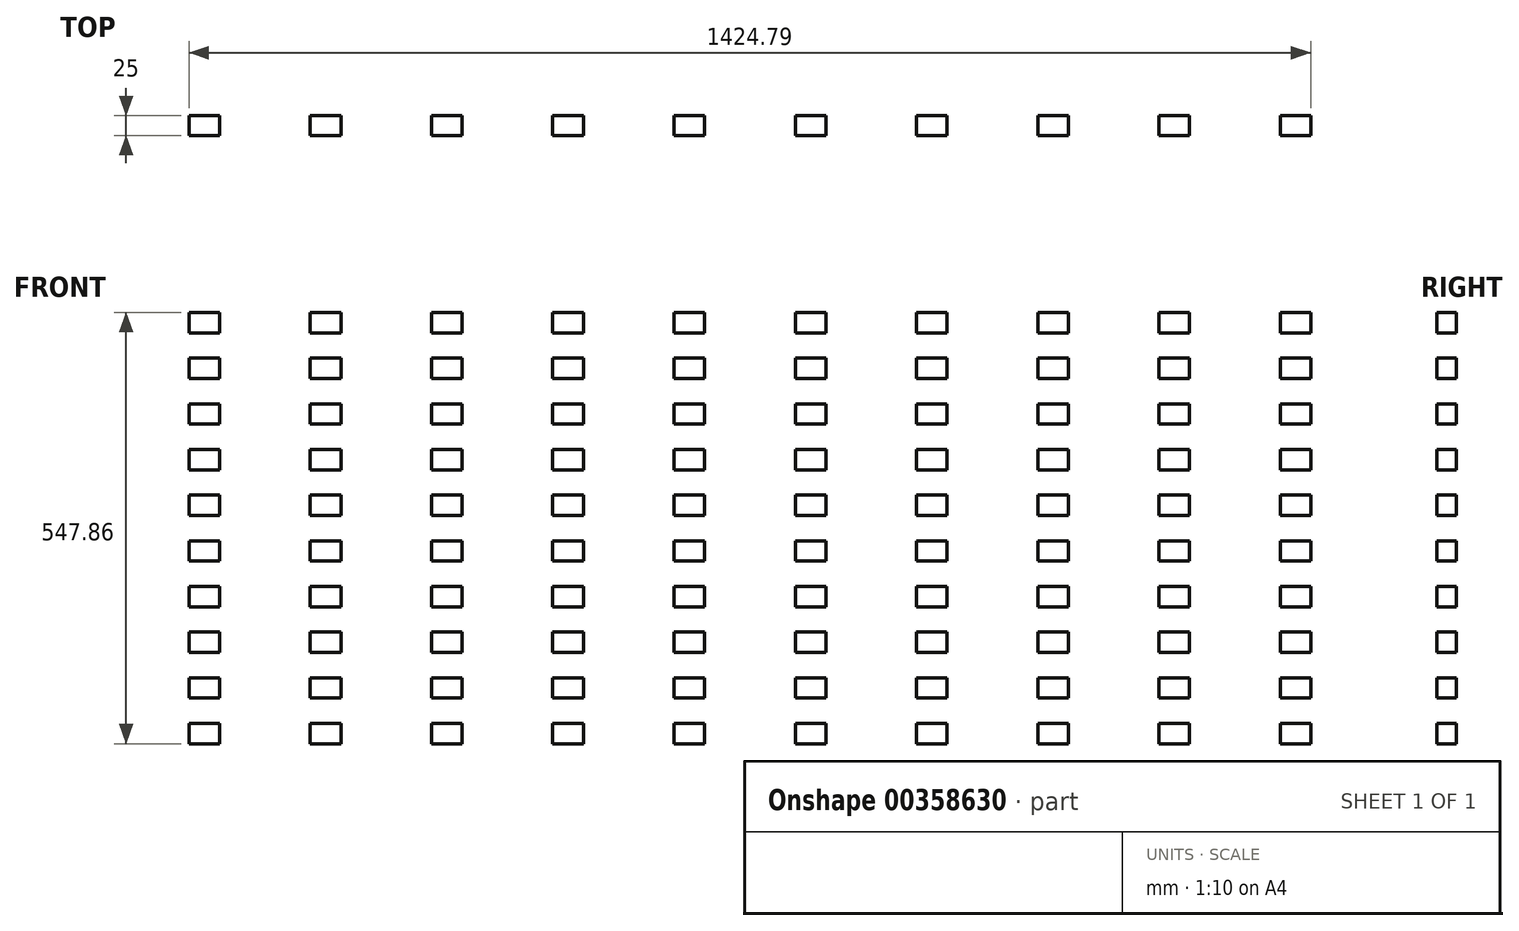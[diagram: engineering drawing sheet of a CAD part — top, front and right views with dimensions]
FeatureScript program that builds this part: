
annotation { "Feature Type Name" : "Feature", "Feature Type Description" : "" }
export const myFeature = defineFeature(function(context is Context, id is Id, definition is map)
    precondition{}
    {
        {
            var Q0;
            Q0=qCreatedBy(makeId("Front.planeOp"),FACE);
            var sketch = newSketch(context, id + "F0", { "sketchPlane" : qUnion([Q0])});
            skLineSegment(sketch, "E0.bottom", {"start": v(-176.52, 30.36) * mm, "end": v(-137.73, 30.36) * mm});
            skLineSegment(sketch, "E0.top", {"start": v(-176.52, 4.5) * mm, "end": v(-137.73, 4.5) * mm});
            skLineSegment(sketch, "E0.left", {"start": v(-176.52, 30.36) * mm, "end": v(-176.52, 4.5) * mm});
            skLineSegment(sketch, "E0.right", {"start": v(-137.73, 30.36) * mm, "end": v(-137.73, 4.5) * mm});
            skLineSegment(sketch, "E1.0.1.0", {"start": v(-176.52, 88.36) * mm, "end": v(-137.73, 88.36) * mm});
            skLineSegment(sketch, "E1.0.1.1", {"start": v(-176.52, 62.5) * mm, "end": v(-137.73, 62.5) * mm});
            skLineSegment(sketch, "E1.0.1.2", {"start": v(-176.52, 88.36) * mm, "end": v(-176.52, 62.5) * mm});
            skLineSegment(sketch, "E1.0.1.3", {"start": v(-137.73, 88.36) * mm, "end": v(-137.73, 62.5) * mm});
            skLineSegment(sketch, "E1.0.2.0", {"start": v(-176.52, 146.36) * mm, "end": v(-137.73, 146.36) * mm});
            skLineSegment(sketch, "E1.0.2.1", {"start": v(-176.52, 120.5) * mm, "end": v(-137.73, 120.5) * mm});
            skLineSegment(sketch, "E1.0.2.2", {"start": v(-176.52, 146.36) * mm, "end": v(-176.52, 120.5) * mm});
            skLineSegment(sketch, "E1.0.2.3", {"start": v(-137.73, 146.36) * mm, "end": v(-137.73, 120.5) * mm});
            skLineSegment(sketch, "E1.0.3.0", {"start": v(-176.52, 204.36) * mm, "end": v(-137.73, 204.36) * mm});
            skLineSegment(sketch, "E1.0.3.1", {"start": v(-176.52, 178.5) * mm, "end": v(-137.73, 178.5) * mm});
            skLineSegment(sketch, "E1.0.3.2", {"start": v(-176.52, 204.36) * mm, "end": v(-176.52, 178.5) * mm});
            skLineSegment(sketch, "E1.0.3.3", {"start": v(-137.73, 204.36) * mm, "end": v(-137.73, 178.5) * mm});
            skLineSegment(sketch, "E1.0.4.0", {"start": v(-176.52, 262.36) * mm, "end": v(-137.73, 262.36) * mm});
            skLineSegment(sketch, "E1.0.4.1", {"start": v(-176.52, 236.5) * mm, "end": v(-137.73, 236.5) * mm});
            skLineSegment(sketch, "E1.0.4.2", {"start": v(-176.52, 262.36) * mm, "end": v(-176.52, 236.5) * mm});
            skLineSegment(sketch, "E1.0.4.3", {"start": v(-137.73, 262.36) * mm, "end": v(-137.73, 236.5) * mm});
            skLineSegment(sketch, "E1.0.5.0", {"start": v(-176.52, 320.36) * mm, "end": v(-137.73, 320.36) * mm});
            skLineSegment(sketch, "E1.0.5.1", {"start": v(-176.52, 294.5) * mm, "end": v(-137.73, 294.5) * mm});
            skLineSegment(sketch, "E1.0.5.2", {"start": v(-176.52, 320.36) * mm, "end": v(-176.52, 294.5) * mm});
            skLineSegment(sketch, "E1.0.5.3", {"start": v(-137.73, 320.36) * mm, "end": v(-137.73, 294.5) * mm});
            skLineSegment(sketch, "E1.0.6.0", {"start": v(-176.52, 378.36) * mm, "end": v(-137.73, 378.36) * mm});
            skLineSegment(sketch, "E1.0.6.1", {"start": v(-176.52, 352.5) * mm, "end": v(-137.73, 352.5) * mm});
            skLineSegment(sketch, "E1.0.6.2", {"start": v(-176.52, 378.36) * mm, "end": v(-176.52, 352.5) * mm});
            skLineSegment(sketch, "E1.0.6.3", {"start": v(-137.73, 378.36) * mm, "end": v(-137.73, 352.5) * mm});
            skLineSegment(sketch, "E1.0.7.0", {"start": v(-176.52, 436.36) * mm, "end": v(-137.73, 436.36) * mm});
            skLineSegment(sketch, "E1.0.7.1", {"start": v(-176.52, 410.5) * mm, "end": v(-137.73, 410.5) * mm});
            skLineSegment(sketch, "E1.0.7.2", {"start": v(-176.52, 436.36) * mm, "end": v(-176.52, 410.5) * mm});
            skLineSegment(sketch, "E1.0.7.3", {"start": v(-137.73, 436.36) * mm, "end": v(-137.73, 410.5) * mm});
            skLineSegment(sketch, "E1.0.8.0", {"start": v(-176.52, 494.36) * mm, "end": v(-137.73, 494.36) * mm});
            skLineSegment(sketch, "E1.0.8.1", {"start": v(-176.52, 468.5) * mm, "end": v(-137.73, 468.5) * mm});
            skLineSegment(sketch, "E1.0.8.2", {"start": v(-176.52, 494.36) * mm, "end": v(-176.52, 468.5) * mm});
            skLineSegment(sketch, "E1.0.8.3", {"start": v(-137.73, 494.36) * mm, "end": v(-137.73, 468.5) * mm});
            skLineSegment(sketch, "E1.0.9.0", {"start": v(-176.52, 552.36) * mm, "end": v(-137.73, 552.36) * mm});
            skLineSegment(sketch, "E1.0.9.1", {"start": v(-176.52, 526.5) * mm, "end": v(-137.73, 526.5) * mm});
            skLineSegment(sketch, "E1.0.9.2", {"start": v(-176.52, 552.36) * mm, "end": v(-176.52, 526.5) * mm});
            skLineSegment(sketch, "E1.0.9.3", {"start": v(-137.73, 552.36) * mm, "end": v(-137.73, 526.5) * mm});
            skLineSegment(sketch, "E1.1.0.0", {"start": v(-22.52, 30.36) * mm, "end": v(16.27, 30.36) * mm});
            skLineSegment(sketch, "E1.1.0.1", {"start": v(-22.52, 4.5) * mm, "end": v(16.27, 4.5) * mm});
            skLineSegment(sketch, "E1.1.0.2", {"start": v(-22.52, 30.36) * mm, "end": v(-22.52, 4.5) * mm});
            skLineSegment(sketch, "E1.1.0.3", {"start": v(16.27, 30.36) * mm, "end": v(16.27, 4.5) * mm});
            skLineSegment(sketch, "E1.1.1.0", {"start": v(-22.52, 88.36) * mm, "end": v(16.27, 88.36) * mm});
            skLineSegment(sketch, "E1.1.1.1", {"start": v(-22.52, 62.5) * mm, "end": v(16.27, 62.5) * mm});
            skLineSegment(sketch, "E1.1.1.2", {"start": v(-22.52, 88.36) * mm, "end": v(-22.52, 62.5) * mm});
            skLineSegment(sketch, "E1.1.1.3", {"start": v(16.27, 88.36) * mm, "end": v(16.27, 62.5) * mm});
            skLineSegment(sketch, "E1.1.2.0", {"start": v(-22.52, 146.36) * mm, "end": v(16.27, 146.36) * mm});
            skLineSegment(sketch, "E1.1.2.1", {"start": v(-22.52, 120.5) * mm, "end": v(16.27, 120.5) * mm});
            skLineSegment(sketch, "E1.1.2.2", {"start": v(-22.52, 146.36) * mm, "end": v(-22.52, 120.5) * mm});
            skLineSegment(sketch, "E1.1.2.3", {"start": v(16.27, 146.36) * mm, "end": v(16.27, 120.5) * mm});
            skLineSegment(sketch, "E1.1.3.0", {"start": v(-22.52, 204.36) * mm, "end": v(16.27, 204.36) * mm});
            skLineSegment(sketch, "E1.1.3.1", {"start": v(-22.52, 178.5) * mm, "end": v(16.27, 178.5) * mm});
            skLineSegment(sketch, "E1.1.3.2", {"start": v(-22.52, 204.36) * mm, "end": v(-22.52, 178.5) * mm});
            skLineSegment(sketch, "E1.1.3.3", {"start": v(16.27, 204.36) * mm, "end": v(16.27, 178.5) * mm});
            skLineSegment(sketch, "E1.1.4.0", {"start": v(-22.52, 262.36) * mm, "end": v(16.27, 262.36) * mm});
            skLineSegment(sketch, "E1.1.4.1", {"start": v(-22.52, 236.5) * mm, "end": v(16.27, 236.5) * mm});
            skLineSegment(sketch, "E1.1.4.2", {"start": v(-22.52, 262.36) * mm, "end": v(-22.52, 236.5) * mm});
            skLineSegment(sketch, "E1.1.4.3", {"start": v(16.27, 262.36) * mm, "end": v(16.27, 236.5) * mm});
            skLineSegment(sketch, "E1.1.5.0", {"start": v(-22.52, 320.36) * mm, "end": v(16.27, 320.36) * mm});
            skLineSegment(sketch, "E1.1.5.1", {"start": v(-22.52, 294.5) * mm, "end": v(16.27, 294.5) * mm});
            skLineSegment(sketch, "E1.1.5.2", {"start": v(-22.52, 320.36) * mm, "end": v(-22.52, 294.5) * mm});
            skLineSegment(sketch, "E1.1.5.3", {"start": v(16.27, 320.36) * mm, "end": v(16.27, 294.5) * mm});
            skLineSegment(sketch, "E1.1.6.0", {"start": v(-22.52, 378.36) * mm, "end": v(16.27, 378.36) * mm});
            skLineSegment(sketch, "E1.1.6.1", {"start": v(-22.52, 352.5) * mm, "end": v(16.27, 352.5) * mm});
            skLineSegment(sketch, "E1.1.6.2", {"start": v(-22.52, 378.36) * mm, "end": v(-22.52, 352.5) * mm});
            skLineSegment(sketch, "E1.1.6.3", {"start": v(16.27, 378.36) * mm, "end": v(16.27, 352.5) * mm});
            skLineSegment(sketch, "E1.1.7.0", {"start": v(-22.52, 436.36) * mm, "end": v(16.27, 436.36) * mm});
            skLineSegment(sketch, "E1.1.7.1", {"start": v(-22.52, 410.5) * mm, "end": v(16.27, 410.5) * mm});
            skLineSegment(sketch, "E1.1.7.2", {"start": v(-22.52, 436.36) * mm, "end": v(-22.52, 410.5) * mm});
            skLineSegment(sketch, "E1.1.7.3", {"start": v(16.27, 436.36) * mm, "end": v(16.27, 410.5) * mm});
            skLineSegment(sketch, "E1.1.8.0", {"start": v(-22.52, 494.36) * mm, "end": v(16.27, 494.36) * mm});
            skLineSegment(sketch, "E1.1.8.1", {"start": v(-22.52, 468.5) * mm, "end": v(16.27, 468.5) * mm});
            skLineSegment(sketch, "E1.1.8.2", {"start": v(-22.52, 494.36) * mm, "end": v(-22.52, 468.5) * mm});
            skLineSegment(sketch, "E1.1.8.3", {"start": v(16.27, 494.36) * mm, "end": v(16.27, 468.5) * mm});
            skLineSegment(sketch, "E1.1.9.0", {"start": v(-22.52, 552.36) * mm, "end": v(16.27, 552.36) * mm});
            skLineSegment(sketch, "E1.1.9.1", {"start": v(-22.52, 526.5) * mm, "end": v(16.27, 526.5) * mm});
            skLineSegment(sketch, "E1.1.9.2", {"start": v(-22.52, 552.36) * mm, "end": v(-22.52, 526.5) * mm});
            skLineSegment(sketch, "E1.1.9.3", {"start": v(16.27, 552.36) * mm, "end": v(16.27, 526.5) * mm});
            skLineSegment(sketch, "E1.2.0.0", {"start": v(131.48, 30.36) * mm, "end": v(170.27, 30.36) * mm});
            skLineSegment(sketch, "E1.2.0.1", {"start": v(131.48, 4.5) * mm, "end": v(170.27, 4.5) * mm});
            skLineSegment(sketch, "E1.2.0.2", {"start": v(131.48, 30.36) * mm, "end": v(131.48, 4.5) * mm});
            skLineSegment(sketch, "E1.2.0.3", {"start": v(170.27, 30.36) * mm, "end": v(170.27, 4.5) * mm});
            skLineSegment(sketch, "E1.2.1.0", {"start": v(131.48, 88.36) * mm, "end": v(170.27, 88.36) * mm});
            skLineSegment(sketch, "E1.2.1.1", {"start": v(131.48, 62.5) * mm, "end": v(170.27, 62.5) * mm});
            skLineSegment(sketch, "E1.2.1.2", {"start": v(131.48, 88.36) * mm, "end": v(131.48, 62.5) * mm});
            skLineSegment(sketch, "E1.2.1.3", {"start": v(170.27, 88.36) * mm, "end": v(170.27, 62.5) * mm});
            skLineSegment(sketch, "E1.2.2.0", {"start": v(131.48, 146.36) * mm, "end": v(170.27, 146.36) * mm});
            skLineSegment(sketch, "E1.2.2.1", {"start": v(131.48, 120.5) * mm, "end": v(170.27, 120.5) * mm});
            skLineSegment(sketch, "E1.2.2.2", {"start": v(131.48, 146.36) * mm, "end": v(131.48, 120.5) * mm});
            skLineSegment(sketch, "E1.2.2.3", {"start": v(170.27, 146.36) * mm, "end": v(170.27, 120.5) * mm});
            skLineSegment(sketch, "E1.2.3.0", {"start": v(131.48, 204.36) * mm, "end": v(170.27, 204.36) * mm});
            skLineSegment(sketch, "E1.2.3.1", {"start": v(131.48, 178.5) * mm, "end": v(170.27, 178.5) * mm});
            skLineSegment(sketch, "E1.2.3.2", {"start": v(131.48, 204.36) * mm, "end": v(131.48, 178.5) * mm});
            skLineSegment(sketch, "E1.2.3.3", {"start": v(170.27, 204.36) * mm, "end": v(170.27, 178.5) * mm});
            skLineSegment(sketch, "E1.2.4.0", {"start": v(131.48, 262.36) * mm, "end": v(170.27, 262.36) * mm});
            skLineSegment(sketch, "E1.2.4.1", {"start": v(131.48, 236.5) * mm, "end": v(170.27, 236.5) * mm});
            skLineSegment(sketch, "E1.2.4.2", {"start": v(131.48, 262.36) * mm, "end": v(131.48, 236.5) * mm});
            skLineSegment(sketch, "E1.2.4.3", {"start": v(170.27, 262.36) * mm, "end": v(170.27, 236.5) * mm});
            skLineSegment(sketch, "E1.2.5.0", {"start": v(131.48, 320.36) * mm, "end": v(170.27, 320.36) * mm});
            skLineSegment(sketch, "E1.2.5.1", {"start": v(131.48, 294.5) * mm, "end": v(170.27, 294.5) * mm});
            skLineSegment(sketch, "E1.2.5.2", {"start": v(131.48, 320.36) * mm, "end": v(131.48, 294.5) * mm});
            skLineSegment(sketch, "E1.2.5.3", {"start": v(170.27, 320.36) * mm, "end": v(170.27, 294.5) * mm});
            skLineSegment(sketch, "E1.2.6.0", {"start": v(131.48, 378.36) * mm, "end": v(170.27, 378.36) * mm});
            skLineSegment(sketch, "E1.2.6.1", {"start": v(131.48, 352.5) * mm, "end": v(170.27, 352.5) * mm});
            skLineSegment(sketch, "E1.2.6.2", {"start": v(131.48, 378.36) * mm, "end": v(131.48, 352.5) * mm});
            skLineSegment(sketch, "E1.2.6.3", {"start": v(170.27, 378.36) * mm, "end": v(170.27, 352.5) * mm});
            skLineSegment(sketch, "E1.2.7.0", {"start": v(131.48, 436.36) * mm, "end": v(170.27, 436.36) * mm});
            skLineSegment(sketch, "E1.2.7.1", {"start": v(131.48, 410.5) * mm, "end": v(170.27, 410.5) * mm});
            skLineSegment(sketch, "E1.2.7.2", {"start": v(131.48, 436.36) * mm, "end": v(131.48, 410.5) * mm});
            skLineSegment(sketch, "E1.2.7.3", {"start": v(170.27, 436.36) * mm, "end": v(170.27, 410.5) * mm});
            skLineSegment(sketch, "E1.2.8.0", {"start": v(131.48, 494.36) * mm, "end": v(170.27, 494.36) * mm});
            skLineSegment(sketch, "E1.2.8.1", {"start": v(131.48, 468.5) * mm, "end": v(170.27, 468.5) * mm});
            skLineSegment(sketch, "E1.2.8.2", {"start": v(131.48, 494.36) * mm, "end": v(131.48, 468.5) * mm});
            skLineSegment(sketch, "E1.2.8.3", {"start": v(170.27, 494.36) * mm, "end": v(170.27, 468.5) * mm});
            skLineSegment(sketch, "E1.2.9.0", {"start": v(131.48, 552.36) * mm, "end": v(170.27, 552.36) * mm});
            skLineSegment(sketch, "E1.2.9.1", {"start": v(131.48, 526.5) * mm, "end": v(170.27, 526.5) * mm});
            skLineSegment(sketch, "E1.2.9.2", {"start": v(131.48, 552.36) * mm, "end": v(131.48, 526.5) * mm});
            skLineSegment(sketch, "E1.2.9.3", {"start": v(170.27, 552.36) * mm, "end": v(170.27, 526.5) * mm});
            skLineSegment(sketch, "E1.3.0.0", {"start": v(285.48, 30.36) * mm, "end": v(324.27, 30.36) * mm});
            skLineSegment(sketch, "E1.3.0.1", {"start": v(285.48, 4.5) * mm, "end": v(324.27, 4.5) * mm});
            skLineSegment(sketch, "E1.3.0.2", {"start": v(285.48, 30.36) * mm, "end": v(285.48, 4.5) * mm});
            skLineSegment(sketch, "E1.3.0.3", {"start": v(324.27, 30.36) * mm, "end": v(324.27, 4.5) * mm});
            skLineSegment(sketch, "E1.3.1.0", {"start": v(285.48, 88.36) * mm, "end": v(324.27, 88.36) * mm});
            skLineSegment(sketch, "E1.3.1.1", {"start": v(285.48, 62.5) * mm, "end": v(324.27, 62.5) * mm});
            skLineSegment(sketch, "E1.3.1.2", {"start": v(285.48, 88.36) * mm, "end": v(285.48, 62.5) * mm});
            skLineSegment(sketch, "E1.3.1.3", {"start": v(324.27, 88.36) * mm, "end": v(324.27, 62.5) * mm});
            skLineSegment(sketch, "E1.3.2.0", {"start": v(285.48, 146.36) * mm, "end": v(324.27, 146.36) * mm});
            skLineSegment(sketch, "E1.3.2.1", {"start": v(285.48, 120.5) * mm, "end": v(324.27, 120.5) * mm});
            skLineSegment(sketch, "E1.3.2.2", {"start": v(285.48, 146.36) * mm, "end": v(285.48, 120.5) * mm});
            skLineSegment(sketch, "E1.3.2.3", {"start": v(324.27, 146.36) * mm, "end": v(324.27, 120.5) * mm});
            skLineSegment(sketch, "E1.3.3.0", {"start": v(285.48, 204.36) * mm, "end": v(324.27, 204.36) * mm});
            skLineSegment(sketch, "E1.3.3.1", {"start": v(285.48, 178.5) * mm, "end": v(324.27, 178.5) * mm});
            skLineSegment(sketch, "E1.3.3.2", {"start": v(285.48, 204.36) * mm, "end": v(285.48, 178.5) * mm});
            skLineSegment(sketch, "E1.3.3.3", {"start": v(324.27, 204.36) * mm, "end": v(324.27, 178.5) * mm});
            skLineSegment(sketch, "E1.3.4.0", {"start": v(285.48, 262.36) * mm, "end": v(324.27, 262.36) * mm});
            skLineSegment(sketch, "E1.3.4.1", {"start": v(285.48, 236.5) * mm, "end": v(324.27, 236.5) * mm});
            skLineSegment(sketch, "E1.3.4.2", {"start": v(285.48, 262.36) * mm, "end": v(285.48, 236.5) * mm});
            skLineSegment(sketch, "E1.3.4.3", {"start": v(324.27, 262.36) * mm, "end": v(324.27, 236.5) * mm});
            skLineSegment(sketch, "E1.3.5.0", {"start": v(285.48, 320.36) * mm, "end": v(324.27, 320.36) * mm});
            skLineSegment(sketch, "E1.3.5.1", {"start": v(285.48, 294.5) * mm, "end": v(324.27, 294.5) * mm});
            skLineSegment(sketch, "E1.3.5.2", {"start": v(285.48, 320.36) * mm, "end": v(285.48, 294.5) * mm});
            skLineSegment(sketch, "E1.3.5.3", {"start": v(324.27, 320.36) * mm, "end": v(324.27, 294.5) * mm});
            skLineSegment(sketch, "E1.3.6.0", {"start": v(285.48, 378.36) * mm, "end": v(324.27, 378.36) * mm});
            skLineSegment(sketch, "E1.3.6.1", {"start": v(285.48, 352.5) * mm, "end": v(324.27, 352.5) * mm});
            skLineSegment(sketch, "E1.3.6.2", {"start": v(285.48, 378.36) * mm, "end": v(285.48, 352.5) * mm});
            skLineSegment(sketch, "E1.3.6.3", {"start": v(324.27, 378.36) * mm, "end": v(324.27, 352.5) * mm});
            skLineSegment(sketch, "E1.3.7.0", {"start": v(285.48, 436.36) * mm, "end": v(324.27, 436.36) * mm});
            skLineSegment(sketch, "E1.3.7.1", {"start": v(285.48, 410.5) * mm, "end": v(324.27, 410.5) * mm});
            skLineSegment(sketch, "E1.3.7.2", {"start": v(285.48, 436.36) * mm, "end": v(285.48, 410.5) * mm});
            skLineSegment(sketch, "E1.3.7.3", {"start": v(324.27, 436.36) * mm, "end": v(324.27, 410.5) * mm});
            skLineSegment(sketch, "E1.3.8.0", {"start": v(285.48, 494.36) * mm, "end": v(324.27, 494.36) * mm});
            skLineSegment(sketch, "E1.3.8.1", {"start": v(285.48, 468.5) * mm, "end": v(324.27, 468.5) * mm});
            skLineSegment(sketch, "E1.3.8.2", {"start": v(285.48, 494.36) * mm, "end": v(285.48, 468.5) * mm});
            skLineSegment(sketch, "E1.3.8.3", {"start": v(324.27, 494.36) * mm, "end": v(324.27, 468.5) * mm});
            skLineSegment(sketch, "E1.3.9.0", {"start": v(285.48, 552.36) * mm, "end": v(324.27, 552.36) * mm});
            skLineSegment(sketch, "E1.3.9.1", {"start": v(285.48, 526.5) * mm, "end": v(324.27, 526.5) * mm});
            skLineSegment(sketch, "E1.3.9.2", {"start": v(285.48, 552.36) * mm, "end": v(285.48, 526.5) * mm});
            skLineSegment(sketch, "E1.3.9.3", {"start": v(324.27, 552.36) * mm, "end": v(324.27, 526.5) * mm});
            skLineSegment(sketch, "E1.4.0.0", {"start": v(439.48, 30.36) * mm, "end": v(478.27, 30.36) * mm});
            skLineSegment(sketch, "E1.4.0.1", {"start": v(439.48, 4.5) * mm, "end": v(478.27, 4.5) * mm});
            skLineSegment(sketch, "E1.4.0.2", {"start": v(439.48, 30.36) * mm, "end": v(439.48, 4.5) * mm});
            skLineSegment(sketch, "E1.4.0.3", {"start": v(478.27, 30.36) * mm, "end": v(478.27, 4.5) * mm});
            skLineSegment(sketch, "E1.4.1.0", {"start": v(439.48, 88.36) * mm, "end": v(478.27, 88.36) * mm});
            skLineSegment(sketch, "E1.4.1.1", {"start": v(439.48, 62.5) * mm, "end": v(478.27, 62.5) * mm});
            skLineSegment(sketch, "E1.4.1.2", {"start": v(439.48, 88.36) * mm, "end": v(439.48, 62.5) * mm});
            skLineSegment(sketch, "E1.4.1.3", {"start": v(478.27, 88.36) * mm, "end": v(478.27, 62.5) * mm});
            skLineSegment(sketch, "E1.4.2.0", {"start": v(439.48, 146.36) * mm, "end": v(478.27, 146.36) * mm});
            skLineSegment(sketch, "E1.4.2.1", {"start": v(439.48, 120.5) * mm, "end": v(478.27, 120.5) * mm});
            skLineSegment(sketch, "E1.4.2.2", {"start": v(439.48, 146.36) * mm, "end": v(439.48, 120.5) * mm});
            skLineSegment(sketch, "E1.4.2.3", {"start": v(478.27, 146.36) * mm, "end": v(478.27, 120.5) * mm});
            skLineSegment(sketch, "E1.4.3.0", {"start": v(439.48, 204.36) * mm, "end": v(478.27, 204.36) * mm});
            skLineSegment(sketch, "E1.4.3.1", {"start": v(439.48, 178.5) * mm, "end": v(478.27, 178.5) * mm});
            skLineSegment(sketch, "E1.4.3.2", {"start": v(439.48, 204.36) * mm, "end": v(439.48, 178.5) * mm});
            skLineSegment(sketch, "E1.4.3.3", {"start": v(478.27, 204.36) * mm, "end": v(478.27, 178.5) * mm});
            skLineSegment(sketch, "E1.4.4.0", {"start": v(439.48, 262.36) * mm, "end": v(478.27, 262.36) * mm});
            skLineSegment(sketch, "E1.4.4.1", {"start": v(439.48, 236.5) * mm, "end": v(478.27, 236.5) * mm});
            skLineSegment(sketch, "E1.4.4.2", {"start": v(439.48, 262.36) * mm, "end": v(439.48, 236.5) * mm});
            skLineSegment(sketch, "E1.4.4.3", {"start": v(478.27, 262.36) * mm, "end": v(478.27, 236.5) * mm});
            skLineSegment(sketch, "E1.4.5.0", {"start": v(439.48, 320.36) * mm, "end": v(478.27, 320.36) * mm});
            skLineSegment(sketch, "E1.4.5.1", {"start": v(439.48, 294.5) * mm, "end": v(478.27, 294.5) * mm});
            skLineSegment(sketch, "E1.4.5.2", {"start": v(439.48, 320.36) * mm, "end": v(439.48, 294.5) * mm});
            skLineSegment(sketch, "E1.4.5.3", {"start": v(478.27, 320.36) * mm, "end": v(478.27, 294.5) * mm});
            skLineSegment(sketch, "E1.4.6.0", {"start": v(439.48, 378.36) * mm, "end": v(478.27, 378.36) * mm});
            skLineSegment(sketch, "E1.4.6.1", {"start": v(439.48, 352.5) * mm, "end": v(478.27, 352.5) * mm});
            skLineSegment(sketch, "E1.4.6.2", {"start": v(439.48, 378.36) * mm, "end": v(439.48, 352.5) * mm});
            skLineSegment(sketch, "E1.4.6.3", {"start": v(478.27, 378.36) * mm, "end": v(478.27, 352.5) * mm});
            skLineSegment(sketch, "E1.4.7.0", {"start": v(439.48, 436.36) * mm, "end": v(478.27, 436.36) * mm});
            skLineSegment(sketch, "E1.4.7.1", {"start": v(439.48, 410.5) * mm, "end": v(478.27, 410.5) * mm});
            skLineSegment(sketch, "E1.4.7.2", {"start": v(439.48, 436.36) * mm, "end": v(439.48, 410.5) * mm});
            skLineSegment(sketch, "E1.4.7.3", {"start": v(478.27, 436.36) * mm, "end": v(478.27, 410.5) * mm});
            skLineSegment(sketch, "E1.4.8.0", {"start": v(439.48, 494.36) * mm, "end": v(478.27, 494.36) * mm});
            skLineSegment(sketch, "E1.4.8.1", {"start": v(439.48, 468.5) * mm, "end": v(478.27, 468.5) * mm});
            skLineSegment(sketch, "E1.4.8.2", {"start": v(439.48, 494.36) * mm, "end": v(439.48, 468.5) * mm});
            skLineSegment(sketch, "E1.4.8.3", {"start": v(478.27, 494.36) * mm, "end": v(478.27, 468.5) * mm});
            skLineSegment(sketch, "E1.4.9.0", {"start": v(439.48, 552.36) * mm, "end": v(478.27, 552.36) * mm});
            skLineSegment(sketch, "E1.4.9.1", {"start": v(439.48, 526.5) * mm, "end": v(478.27, 526.5) * mm});
            skLineSegment(sketch, "E1.4.9.2", {"start": v(439.48, 552.36) * mm, "end": v(439.48, 526.5) * mm});
            skLineSegment(sketch, "E1.4.9.3", {"start": v(478.27, 552.36) * mm, "end": v(478.27, 526.5) * mm});
            skLineSegment(sketch, "E1.5.0.0", {"start": v(593.48, 30.36) * mm, "end": v(632.27, 30.36) * mm});
            skLineSegment(sketch, "E1.5.0.1", {"start": v(593.48, 4.5) * mm, "end": v(632.27, 4.5) * mm});
            skLineSegment(sketch, "E1.5.0.2", {"start": v(593.48, 30.36) * mm, "end": v(593.48, 4.5) * mm});
            skLineSegment(sketch, "E1.5.0.3", {"start": v(632.27, 30.36) * mm, "end": v(632.27, 4.5) * mm});
            skLineSegment(sketch, "E1.5.1.0", {"start": v(593.48, 88.36) * mm, "end": v(632.27, 88.36) * mm});
            skLineSegment(sketch, "E1.5.1.1", {"start": v(593.48, 62.5) * mm, "end": v(632.27, 62.5) * mm});
            skLineSegment(sketch, "E1.5.1.2", {"start": v(593.48, 88.36) * mm, "end": v(593.48, 62.5) * mm});
            skLineSegment(sketch, "E1.5.1.3", {"start": v(632.27, 88.36) * mm, "end": v(632.27, 62.5) * mm});
            skLineSegment(sketch, "E1.5.2.0", {"start": v(593.48, 146.36) * mm, "end": v(632.27, 146.36) * mm});
            skLineSegment(sketch, "E1.5.2.1", {"start": v(593.48, 120.5) * mm, "end": v(632.27, 120.5) * mm});
            skLineSegment(sketch, "E1.5.2.2", {"start": v(593.48, 146.36) * mm, "end": v(593.48, 120.5) * mm});
            skLineSegment(sketch, "E1.5.2.3", {"start": v(632.27, 146.36) * mm, "end": v(632.27, 120.5) * mm});
            skLineSegment(sketch, "E1.5.3.0", {"start": v(593.48, 204.36) * mm, "end": v(632.27, 204.36) * mm});
            skLineSegment(sketch, "E1.5.3.1", {"start": v(593.48, 178.5) * mm, "end": v(632.27, 178.5) * mm});
            skLineSegment(sketch, "E1.5.3.2", {"start": v(593.48, 204.36) * mm, "end": v(593.48, 178.5) * mm});
            skLineSegment(sketch, "E1.5.3.3", {"start": v(632.27, 204.36) * mm, "end": v(632.27, 178.5) * mm});
            skLineSegment(sketch, "E1.5.4.0", {"start": v(593.48, 262.36) * mm, "end": v(632.27, 262.36) * mm});
            skLineSegment(sketch, "E1.5.4.1", {"start": v(593.48, 236.5) * mm, "end": v(632.27, 236.5) * mm});
            skLineSegment(sketch, "E1.5.4.2", {"start": v(593.48, 262.36) * mm, "end": v(593.48, 236.5) * mm});
            skLineSegment(sketch, "E1.5.4.3", {"start": v(632.27, 262.36) * mm, "end": v(632.27, 236.5) * mm});
            skLineSegment(sketch, "E1.5.5.0", {"start": v(593.48, 320.36) * mm, "end": v(632.27, 320.36) * mm});
            skLineSegment(sketch, "E1.5.5.1", {"start": v(593.48, 294.5) * mm, "end": v(632.27, 294.5) * mm});
            skLineSegment(sketch, "E1.5.5.2", {"start": v(593.48, 320.36) * mm, "end": v(593.48, 294.5) * mm});
            skLineSegment(sketch, "E1.5.5.3", {"start": v(632.27, 320.36) * mm, "end": v(632.27, 294.5) * mm});
            skLineSegment(sketch, "E1.5.6.0", {"start": v(593.48, 378.36) * mm, "end": v(632.27, 378.36) * mm});
            skLineSegment(sketch, "E1.5.6.1", {"start": v(593.48, 352.5) * mm, "end": v(632.27, 352.5) * mm});
            skLineSegment(sketch, "E1.5.6.2", {"start": v(593.48, 378.36) * mm, "end": v(593.48, 352.5) * mm});
            skLineSegment(sketch, "E1.5.6.3", {"start": v(632.27, 378.36) * mm, "end": v(632.27, 352.5) * mm});
            skLineSegment(sketch, "E1.5.7.0", {"start": v(593.48, 436.36) * mm, "end": v(632.27, 436.36) * mm});
            skLineSegment(sketch, "E1.5.7.1", {"start": v(593.48, 410.5) * mm, "end": v(632.27, 410.5) * mm});
            skLineSegment(sketch, "E1.5.7.2", {"start": v(593.48, 436.36) * mm, "end": v(593.48, 410.5) * mm});
            skLineSegment(sketch, "E1.5.7.3", {"start": v(632.27, 436.36) * mm, "end": v(632.27, 410.5) * mm});
            skLineSegment(sketch, "E1.5.8.0", {"start": v(593.48, 494.36) * mm, "end": v(632.27, 494.36) * mm});
            skLineSegment(sketch, "E1.5.8.1", {"start": v(593.48, 468.5) * mm, "end": v(632.27, 468.5) * mm});
            skLineSegment(sketch, "E1.5.8.2", {"start": v(593.48, 494.36) * mm, "end": v(593.48, 468.5) * mm});
            skLineSegment(sketch, "E1.5.8.3", {"start": v(632.27, 494.36) * mm, "end": v(632.27, 468.5) * mm});
            skLineSegment(sketch, "E1.5.9.0", {"start": v(593.48, 552.36) * mm, "end": v(632.27, 552.36) * mm});
            skLineSegment(sketch, "E1.5.9.1", {"start": v(593.48, 526.5) * mm, "end": v(632.27, 526.5) * mm});
            skLineSegment(sketch, "E1.5.9.2", {"start": v(593.48, 552.36) * mm, "end": v(593.48, 526.5) * mm});
            skLineSegment(sketch, "E1.5.9.3", {"start": v(632.27, 552.36) * mm, "end": v(632.27, 526.5) * mm});
            skLineSegment(sketch, "E1.6.0.0", {"start": v(747.48, 30.36) * mm, "end": v(786.27, 30.36) * mm});
            skLineSegment(sketch, "E1.6.0.1", {"start": v(747.48, 4.5) * mm, "end": v(786.27, 4.5) * mm});
            skLineSegment(sketch, "E1.6.0.2", {"start": v(747.48, 30.36) * mm, "end": v(747.48, 4.5) * mm});
            skLineSegment(sketch, "E1.6.0.3", {"start": v(786.27, 30.36) * mm, "end": v(786.27, 4.5) * mm});
            skLineSegment(sketch, "E1.6.1.0", {"start": v(747.48, 88.36) * mm, "end": v(786.27, 88.36) * mm});
            skLineSegment(sketch, "E1.6.1.1", {"start": v(747.48, 62.5) * mm, "end": v(786.27, 62.5) * mm});
            skLineSegment(sketch, "E1.6.1.2", {"start": v(747.48, 88.36) * mm, "end": v(747.48, 62.5) * mm});
            skLineSegment(sketch, "E1.6.1.3", {"start": v(786.27, 88.36) * mm, "end": v(786.27, 62.5) * mm});
            skLineSegment(sketch, "E1.6.2.0", {"start": v(747.48, 146.36) * mm, "end": v(786.27, 146.36) * mm});
            skLineSegment(sketch, "E1.6.2.1", {"start": v(747.48, 120.5) * mm, "end": v(786.27, 120.5) * mm});
            skLineSegment(sketch, "E1.6.2.2", {"start": v(747.48, 146.36) * mm, "end": v(747.48, 120.5) * mm});
            skLineSegment(sketch, "E1.6.2.3", {"start": v(786.27, 146.36) * mm, "end": v(786.27, 120.5) * mm});
            skLineSegment(sketch, "E1.6.3.0", {"start": v(747.48, 204.36) * mm, "end": v(786.27, 204.36) * mm});
            skLineSegment(sketch, "E1.6.3.1", {"start": v(747.48, 178.5) * mm, "end": v(786.27, 178.5) * mm});
            skLineSegment(sketch, "E1.6.3.2", {"start": v(747.48, 204.36) * mm, "end": v(747.48, 178.5) * mm});
            skLineSegment(sketch, "E1.6.3.3", {"start": v(786.27, 204.36) * mm, "end": v(786.27, 178.5) * mm});
            skLineSegment(sketch, "E1.6.4.0", {"start": v(747.48, 262.36) * mm, "end": v(786.27, 262.36) * mm});
            skLineSegment(sketch, "E1.6.4.1", {"start": v(747.48, 236.5) * mm, "end": v(786.27, 236.5) * mm});
            skLineSegment(sketch, "E1.6.4.2", {"start": v(747.48, 262.36) * mm, "end": v(747.48, 236.5) * mm});
            skLineSegment(sketch, "E1.6.4.3", {"start": v(786.27, 262.36) * mm, "end": v(786.27, 236.5) * mm});
            skLineSegment(sketch, "E1.6.5.0", {"start": v(747.48, 320.36) * mm, "end": v(786.27, 320.36) * mm});
            skLineSegment(sketch, "E1.6.5.1", {"start": v(747.48, 294.5) * mm, "end": v(786.27, 294.5) * mm});
            skLineSegment(sketch, "E1.6.5.2", {"start": v(747.48, 320.36) * mm, "end": v(747.48, 294.5) * mm});
            skLineSegment(sketch, "E1.6.5.3", {"start": v(786.27, 320.36) * mm, "end": v(786.27, 294.5) * mm});
            skLineSegment(sketch, "E1.6.6.0", {"start": v(747.48, 378.36) * mm, "end": v(786.27, 378.36) * mm});
            skLineSegment(sketch, "E1.6.6.1", {"start": v(747.48, 352.5) * mm, "end": v(786.27, 352.5) * mm});
            skLineSegment(sketch, "E1.6.6.2", {"start": v(747.48, 378.36) * mm, "end": v(747.48, 352.5) * mm});
            skLineSegment(sketch, "E1.6.6.3", {"start": v(786.27, 378.36) * mm, "end": v(786.27, 352.5) * mm});
            skLineSegment(sketch, "E1.6.7.0", {"start": v(747.48, 436.36) * mm, "end": v(786.27, 436.36) * mm});
            skLineSegment(sketch, "E1.6.7.1", {"start": v(747.48, 410.5) * mm, "end": v(786.27, 410.5) * mm});
            skLineSegment(sketch, "E1.6.7.2", {"start": v(747.48, 436.36) * mm, "end": v(747.48, 410.5) * mm});
            skLineSegment(sketch, "E1.6.7.3", {"start": v(786.27, 436.36) * mm, "end": v(786.27, 410.5) * mm});
            skLineSegment(sketch, "E1.6.8.0", {"start": v(747.48, 494.36) * mm, "end": v(786.27, 494.36) * mm});
            skLineSegment(sketch, "E1.6.8.1", {"start": v(747.48, 468.5) * mm, "end": v(786.27, 468.5) * mm});
            skLineSegment(sketch, "E1.6.8.2", {"start": v(747.48, 494.36) * mm, "end": v(747.48, 468.5) * mm});
            skLineSegment(sketch, "E1.6.8.3", {"start": v(786.27, 494.36) * mm, "end": v(786.27, 468.5) * mm});
            skLineSegment(sketch, "E1.6.9.0", {"start": v(747.48, 552.36) * mm, "end": v(786.27, 552.36) * mm});
            skLineSegment(sketch, "E1.6.9.1", {"start": v(747.48, 526.5) * mm, "end": v(786.27, 526.5) * mm});
            skLineSegment(sketch, "E1.6.9.2", {"start": v(747.48, 552.36) * mm, "end": v(747.48, 526.5) * mm});
            skLineSegment(sketch, "E1.6.9.3", {"start": v(786.27, 552.36) * mm, "end": v(786.27, 526.5) * mm});
            skLineSegment(sketch, "E1.7.0.0", {"start": v(901.48, 30.36) * mm, "end": v(940.27, 30.36) * mm});
            skLineSegment(sketch, "E1.7.0.1", {"start": v(901.48, 4.5) * mm, "end": v(940.27, 4.5) * mm});
            skLineSegment(sketch, "E1.7.0.2", {"start": v(901.48, 30.36) * mm, "end": v(901.48, 4.5) * mm});
            skLineSegment(sketch, "E1.7.0.3", {"start": v(940.27, 30.36) * mm, "end": v(940.27, 4.5) * mm});
            skLineSegment(sketch, "E1.7.1.0", {"start": v(901.48, 88.36) * mm, "end": v(940.27, 88.36) * mm});
            skLineSegment(sketch, "E1.7.1.1", {"start": v(901.48, 62.5) * mm, "end": v(940.27, 62.5) * mm});
            skLineSegment(sketch, "E1.7.1.2", {"start": v(901.48, 88.36) * mm, "end": v(901.48, 62.5) * mm});
            skLineSegment(sketch, "E1.7.1.3", {"start": v(940.27, 88.36) * mm, "end": v(940.27, 62.5) * mm});
            skLineSegment(sketch, "E1.7.2.0", {"start": v(901.48, 146.36) * mm, "end": v(940.27, 146.36) * mm});
            skLineSegment(sketch, "E1.7.2.1", {"start": v(901.48, 120.5) * mm, "end": v(940.27, 120.5) * mm});
            skLineSegment(sketch, "E1.7.2.2", {"start": v(901.48, 146.36) * mm, "end": v(901.48, 120.5) * mm});
            skLineSegment(sketch, "E1.7.2.3", {"start": v(940.27, 146.36) * mm, "end": v(940.27, 120.5) * mm});
            skLineSegment(sketch, "E1.7.3.0", {"start": v(901.48, 204.36) * mm, "end": v(940.27, 204.36) * mm});
            skLineSegment(sketch, "E1.7.3.1", {"start": v(901.48, 178.5) * mm, "end": v(940.27, 178.5) * mm});
            skLineSegment(sketch, "E1.7.3.2", {"start": v(901.48, 204.36) * mm, "end": v(901.48, 178.5) * mm});
            skLineSegment(sketch, "E1.7.3.3", {"start": v(940.27, 204.36) * mm, "end": v(940.27, 178.5) * mm});
            skLineSegment(sketch, "E1.7.4.0", {"start": v(901.48, 262.36) * mm, "end": v(940.27, 262.36) * mm});
            skLineSegment(sketch, "E1.7.4.1", {"start": v(901.48, 236.5) * mm, "end": v(940.27, 236.5) * mm});
            skLineSegment(sketch, "E1.7.4.2", {"start": v(901.48, 262.36) * mm, "end": v(901.48, 236.5) * mm});
            skLineSegment(sketch, "E1.7.4.3", {"start": v(940.27, 262.36) * mm, "end": v(940.27, 236.5) * mm});
            skLineSegment(sketch, "E1.7.5.0", {"start": v(901.48, 320.36) * mm, "end": v(940.27, 320.36) * mm});
            skLineSegment(sketch, "E1.7.5.1", {"start": v(901.48, 294.5) * mm, "end": v(940.27, 294.5) * mm});
            skLineSegment(sketch, "E1.7.5.2", {"start": v(901.48, 320.36) * mm, "end": v(901.48, 294.5) * mm});
            skLineSegment(sketch, "E1.7.5.3", {"start": v(940.27, 320.36) * mm, "end": v(940.27, 294.5) * mm});
            skLineSegment(sketch, "E1.7.6.0", {"start": v(901.48, 378.36) * mm, "end": v(940.27, 378.36) * mm});
            skLineSegment(sketch, "E1.7.6.1", {"start": v(901.48, 352.5) * mm, "end": v(940.27, 352.5) * mm});
            skLineSegment(sketch, "E1.7.6.2", {"start": v(901.48, 378.36) * mm, "end": v(901.48, 352.5) * mm});
            skLineSegment(sketch, "E1.7.6.3", {"start": v(940.27, 378.36) * mm, "end": v(940.27, 352.5) * mm});
            skLineSegment(sketch, "E1.7.7.0", {"start": v(901.48, 436.36) * mm, "end": v(940.27, 436.36) * mm});
            skLineSegment(sketch, "E1.7.7.1", {"start": v(901.48, 410.5) * mm, "end": v(940.27, 410.5) * mm});
            skLineSegment(sketch, "E1.7.7.2", {"start": v(901.48, 436.36) * mm, "end": v(901.48, 410.5) * mm});
            skLineSegment(sketch, "E1.7.7.3", {"start": v(940.27, 436.36) * mm, "end": v(940.27, 410.5) * mm});
            skLineSegment(sketch, "E1.7.8.0", {"start": v(901.48, 494.36) * mm, "end": v(940.27, 494.36) * mm});
            skLineSegment(sketch, "E1.7.8.1", {"start": v(901.48, 468.5) * mm, "end": v(940.27, 468.5) * mm});
            skLineSegment(sketch, "E1.7.8.2", {"start": v(901.48, 494.36) * mm, "end": v(901.48, 468.5) * mm});
            skLineSegment(sketch, "E1.7.8.3", {"start": v(940.27, 494.36) * mm, "end": v(940.27, 468.5) * mm});
            skLineSegment(sketch, "E1.7.9.0", {"start": v(901.48, 552.36) * mm, "end": v(940.27, 552.36) * mm});
            skLineSegment(sketch, "E1.7.9.1", {"start": v(901.48, 526.5) * mm, "end": v(940.27, 526.5) * mm});
            skLineSegment(sketch, "E1.7.9.2", {"start": v(901.48, 552.36) * mm, "end": v(901.48, 526.5) * mm});
            skLineSegment(sketch, "E1.7.9.3", {"start": v(940.27, 552.36) * mm, "end": v(940.27, 526.5) * mm});
            skLineSegment(sketch, "E1.8.0.0", {"start": v(1055.48, 30.36) * mm, "end": v(1094.27, 30.36) * mm});
            skLineSegment(sketch, "E1.8.0.1", {"start": v(1055.48, 4.5) * mm, "end": v(1094.27, 4.5) * mm});
            skLineSegment(sketch, "E1.8.0.2", {"start": v(1055.48, 30.36) * mm, "end": v(1055.48, 4.5) * mm});
            skLineSegment(sketch, "E1.8.0.3", {"start": v(1094.27, 30.36) * mm, "end": v(1094.27, 4.5) * mm});
            skLineSegment(sketch, "E1.8.1.0", {"start": v(1055.48, 88.36) * mm, "end": v(1094.27, 88.36) * mm});
            skLineSegment(sketch, "E1.8.1.1", {"start": v(1055.48, 62.5) * mm, "end": v(1094.27, 62.5) * mm});
            skLineSegment(sketch, "E1.8.1.2", {"start": v(1055.48, 88.36) * mm, "end": v(1055.48, 62.5) * mm});
            skLineSegment(sketch, "E1.8.1.3", {"start": v(1094.27, 88.36) * mm, "end": v(1094.27, 62.5) * mm});
            skLineSegment(sketch, "E1.8.2.0", {"start": v(1055.48, 146.36) * mm, "end": v(1094.27, 146.36) * mm});
            skLineSegment(sketch, "E1.8.2.1", {"start": v(1055.48, 120.5) * mm, "end": v(1094.27, 120.5) * mm});
            skLineSegment(sketch, "E1.8.2.2", {"start": v(1055.48, 146.36) * mm, "end": v(1055.48, 120.5) * mm});
            skLineSegment(sketch, "E1.8.2.3", {"start": v(1094.27, 146.36) * mm, "end": v(1094.27, 120.5) * mm});
            skLineSegment(sketch, "E1.8.3.0", {"start": v(1055.48, 204.36) * mm, "end": v(1094.27, 204.36) * mm});
            skLineSegment(sketch, "E1.8.3.1", {"start": v(1055.48, 178.5) * mm, "end": v(1094.27, 178.5) * mm});
            skLineSegment(sketch, "E1.8.3.2", {"start": v(1055.48, 204.36) * mm, "end": v(1055.48, 178.5) * mm});
            skLineSegment(sketch, "E1.8.3.3", {"start": v(1094.27, 204.36) * mm, "end": v(1094.27, 178.5) * mm});
            skLineSegment(sketch, "E1.8.4.0", {"start": v(1055.48, 262.36) * mm, "end": v(1094.27, 262.36) * mm});
            skLineSegment(sketch, "E1.8.4.1", {"start": v(1055.48, 236.5) * mm, "end": v(1094.27, 236.5) * mm});
            skLineSegment(sketch, "E1.8.4.2", {"start": v(1055.48, 262.36) * mm, "end": v(1055.48, 236.5) * mm});
            skLineSegment(sketch, "E1.8.4.3", {"start": v(1094.27, 262.36) * mm, "end": v(1094.27, 236.5) * mm});
            skLineSegment(sketch, "E1.8.5.0", {"start": v(1055.48, 320.36) * mm, "end": v(1094.27, 320.36) * mm});
            skLineSegment(sketch, "E1.8.5.1", {"start": v(1055.48, 294.5) * mm, "end": v(1094.27, 294.5) * mm});
            skLineSegment(sketch, "E1.8.5.2", {"start": v(1055.48, 320.36) * mm, "end": v(1055.48, 294.5) * mm});
            skLineSegment(sketch, "E1.8.5.3", {"start": v(1094.27, 320.36) * mm, "end": v(1094.27, 294.5) * mm});
            skLineSegment(sketch, "E1.8.6.0", {"start": v(1055.48, 378.36) * mm, "end": v(1094.27, 378.36) * mm});
            skLineSegment(sketch, "E1.8.6.1", {"start": v(1055.48, 352.5) * mm, "end": v(1094.27, 352.5) * mm});
            skLineSegment(sketch, "E1.8.6.2", {"start": v(1055.48, 378.36) * mm, "end": v(1055.48, 352.5) * mm});
            skLineSegment(sketch, "E1.8.6.3", {"start": v(1094.27, 378.36) * mm, "end": v(1094.27, 352.5) * mm});
            skLineSegment(sketch, "E1.8.7.0", {"start": v(1055.48, 436.36) * mm, "end": v(1094.27, 436.36) * mm});
            skLineSegment(sketch, "E1.8.7.1", {"start": v(1055.48, 410.5) * mm, "end": v(1094.27, 410.5) * mm});
            skLineSegment(sketch, "E1.8.7.2", {"start": v(1055.48, 436.36) * mm, "end": v(1055.48, 410.5) * mm});
            skLineSegment(sketch, "E1.8.7.3", {"start": v(1094.27, 436.36) * mm, "end": v(1094.27, 410.5) * mm});
            skLineSegment(sketch, "E1.8.8.0", {"start": v(1055.48, 494.36) * mm, "end": v(1094.27, 494.36) * mm});
            skLineSegment(sketch, "E1.8.8.1", {"start": v(1055.48, 468.5) * mm, "end": v(1094.27, 468.5) * mm});
            skLineSegment(sketch, "E1.8.8.2", {"start": v(1055.48, 494.36) * mm, "end": v(1055.48, 468.5) * mm});
            skLineSegment(sketch, "E1.8.8.3", {"start": v(1094.27, 494.36) * mm, "end": v(1094.27, 468.5) * mm});
            skLineSegment(sketch, "E1.8.9.0", {"start": v(1055.48, 552.36) * mm, "end": v(1094.27, 552.36) * mm});
            skLineSegment(sketch, "E1.8.9.1", {"start": v(1055.48, 526.5) * mm, "end": v(1094.27, 526.5) * mm});
            skLineSegment(sketch, "E1.8.9.2", {"start": v(1055.48, 552.36) * mm, "end": v(1055.48, 526.5) * mm});
            skLineSegment(sketch, "E1.8.9.3", {"start": v(1094.27, 552.36) * mm, "end": v(1094.27, 526.5) * mm});
            skLineSegment(sketch, "E1.9.0.0", {"start": v(1209.48, 30.36) * mm, "end": v(1248.27, 30.36) * mm});
            skLineSegment(sketch, "E1.9.0.1", {"start": v(1209.48, 4.5) * mm, "end": v(1248.27, 4.5) * mm});
            skLineSegment(sketch, "E1.9.0.2", {"start": v(1209.48, 30.36) * mm, "end": v(1209.48, 4.5) * mm});
            skLineSegment(sketch, "E1.9.0.3", {"start": v(1248.27, 30.36) * mm, "end": v(1248.27, 4.5) * mm});
            skLineSegment(sketch, "E1.9.1.0", {"start": v(1209.48, 88.36) * mm, "end": v(1248.27, 88.36) * mm});
            skLineSegment(sketch, "E1.9.1.1", {"start": v(1209.48, 62.5) * mm, "end": v(1248.27, 62.5) * mm});
            skLineSegment(sketch, "E1.9.1.2", {"start": v(1209.48, 88.36) * mm, "end": v(1209.48, 62.5) * mm});
            skLineSegment(sketch, "E1.9.1.3", {"start": v(1248.27, 88.36) * mm, "end": v(1248.27, 62.5) * mm});
            skLineSegment(sketch, "E1.9.2.0", {"start": v(1209.48, 146.36) * mm, "end": v(1248.27, 146.36) * mm});
            skLineSegment(sketch, "E1.9.2.1", {"start": v(1209.48, 120.5) * mm, "end": v(1248.27, 120.5) * mm});
            skLineSegment(sketch, "E1.9.2.2", {"start": v(1209.48, 146.36) * mm, "end": v(1209.48, 120.5) * mm});
            skLineSegment(sketch, "E1.9.2.3", {"start": v(1248.27, 146.36) * mm, "end": v(1248.27, 120.5) * mm});
            skLineSegment(sketch, "E1.9.3.0", {"start": v(1209.48, 204.36) * mm, "end": v(1248.27, 204.36) * mm});
            skLineSegment(sketch, "E1.9.3.1", {"start": v(1209.48, 178.5) * mm, "end": v(1248.27, 178.5) * mm});
            skLineSegment(sketch, "E1.9.3.2", {"start": v(1209.48, 204.36) * mm, "end": v(1209.48, 178.5) * mm});
            skLineSegment(sketch, "E1.9.3.3", {"start": v(1248.27, 204.36) * mm, "end": v(1248.27, 178.5) * mm});
            skLineSegment(sketch, "E1.9.4.0", {"start": v(1209.48, 262.36) * mm, "end": v(1248.27, 262.36) * mm});
            skLineSegment(sketch, "E1.9.4.1", {"start": v(1209.48, 236.5) * mm, "end": v(1248.27, 236.5) * mm});
            skLineSegment(sketch, "E1.9.4.2", {"start": v(1209.48, 262.36) * mm, "end": v(1209.48, 236.5) * mm});
            skLineSegment(sketch, "E1.9.4.3", {"start": v(1248.27, 262.36) * mm, "end": v(1248.27, 236.5) * mm});
            skLineSegment(sketch, "E1.9.5.0", {"start": v(1209.48, 320.36) * mm, "end": v(1248.27, 320.36) * mm});
            skLineSegment(sketch, "E1.9.5.1", {"start": v(1209.48, 294.5) * mm, "end": v(1248.27, 294.5) * mm});
            skLineSegment(sketch, "E1.9.5.2", {"start": v(1209.48, 320.36) * mm, "end": v(1209.48, 294.5) * mm});
            skLineSegment(sketch, "E1.9.5.3", {"start": v(1248.27, 320.36) * mm, "end": v(1248.27, 294.5) * mm});
            skLineSegment(sketch, "E1.9.6.0", {"start": v(1209.48, 378.36) * mm, "end": v(1248.27, 378.36) * mm});
            skLineSegment(sketch, "E1.9.6.1", {"start": v(1209.48, 352.5) * mm, "end": v(1248.27, 352.5) * mm});
            skLineSegment(sketch, "E1.9.6.2", {"start": v(1209.48, 378.36) * mm, "end": v(1209.48, 352.5) * mm});
            skLineSegment(sketch, "E1.9.6.3", {"start": v(1248.27, 378.36) * mm, "end": v(1248.27, 352.5) * mm});
            skLineSegment(sketch, "E1.9.7.0", {"start": v(1209.48, 436.36) * mm, "end": v(1248.27, 436.36) * mm});
            skLineSegment(sketch, "E1.9.7.1", {"start": v(1209.48, 410.5) * mm, "end": v(1248.27, 410.5) * mm});
            skLineSegment(sketch, "E1.9.7.2", {"start": v(1209.48, 436.36) * mm, "end": v(1209.48, 410.5) * mm});
            skLineSegment(sketch, "E1.9.7.3", {"start": v(1248.27, 436.36) * mm, "end": v(1248.27, 410.5) * mm});
            skLineSegment(sketch, "E1.9.8.0", {"start": v(1209.48, 494.36) * mm, "end": v(1248.27, 494.36) * mm});
            skLineSegment(sketch, "E1.9.8.1", {"start": v(1209.48, 468.5) * mm, "end": v(1248.27, 468.5) * mm});
            skLineSegment(sketch, "E1.9.8.2", {"start": v(1209.48, 494.36) * mm, "end": v(1209.48, 468.5) * mm});
            skLineSegment(sketch, "E1.9.8.3", {"start": v(1248.27, 494.36) * mm, "end": v(1248.27, 468.5) * mm});
            skLineSegment(sketch, "E1.9.9.0", {"start": v(1209.48, 552.36) * mm, "end": v(1248.27, 552.36) * mm});
            skLineSegment(sketch, "E1.9.9.1", {"start": v(1209.48, 526.5) * mm, "end": v(1248.27, 526.5) * mm});
            skLineSegment(sketch, "E1.9.9.2", {"start": v(1209.48, 552.36) * mm, "end": v(1209.48, 526.5) * mm});
            skLineSegment(sketch, "E1.9.9.3", {"start": v(1248.27, 552.36) * mm, "end": v(1248.27, 526.5) * mm});
            skLineSegment(sketch, "E1.direction1", {"start": v(-176.52, 4.5) * mm, "end": v(-22.52, 4.5) * mm, "construction": true});
            skLineSegment(sketch, "E1.direction2", {"start": v(-176.52, 4.5) * mm, "end": v(-176.52, 62.5) * mm, "construction": true});
            skSolve(sketch);
        }
        {
            var Q0;
            Q0 = qSketchRegion(id + "F0", true);
            extrude(context, id + "F1", {"entities" : qUnion([Q0]), "depth" : 25 * mm});
        }
    });
